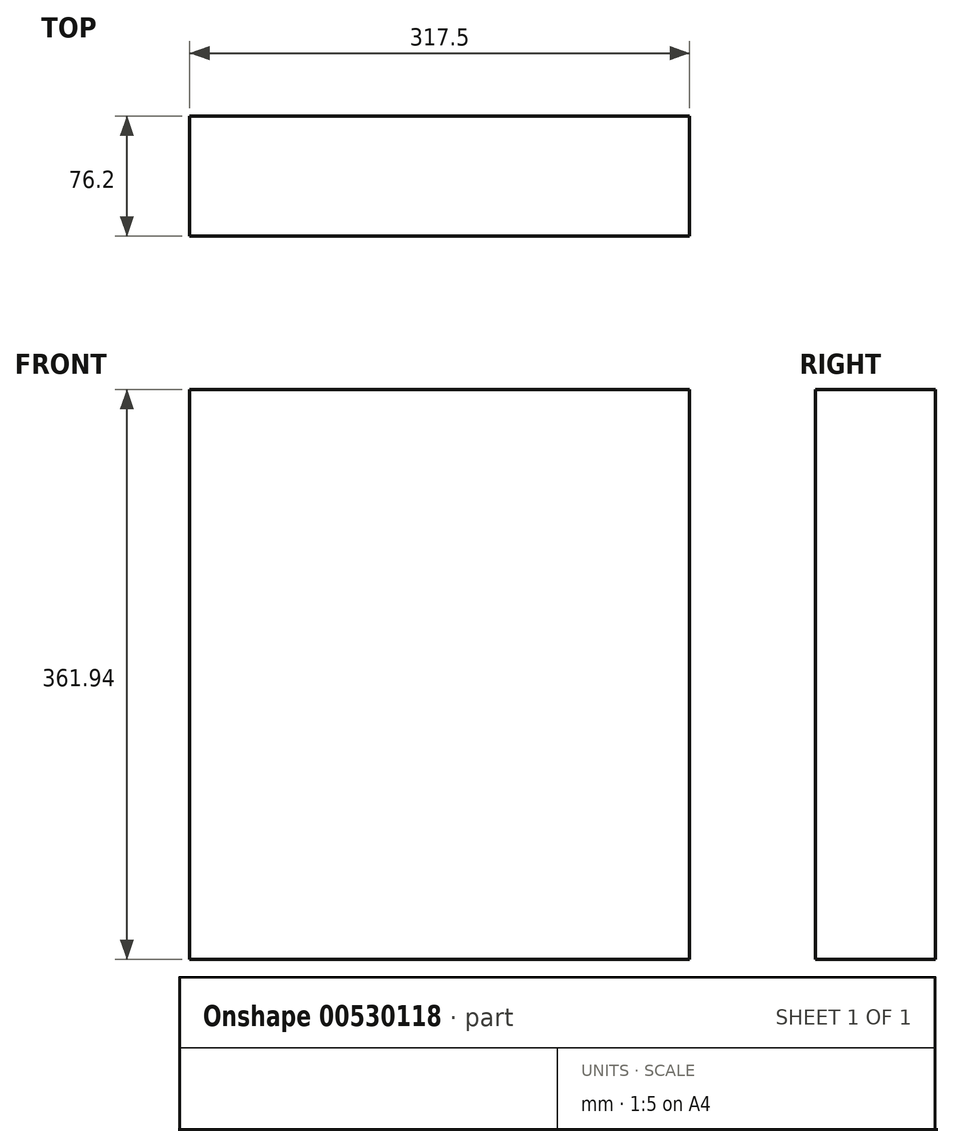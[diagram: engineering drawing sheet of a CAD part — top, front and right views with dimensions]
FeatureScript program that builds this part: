
annotation { "Feature Type Name" : "Feature", "Feature Type Description" : "" }
export const myFeature = defineFeature(function(context is Context, id is Id, definition is map)
    precondition{}
    {
        {
            var Q0;
            Q0=qCreatedBy(makeId("Front.planeOp"),FACE);
            var sketch = newSketch(context, id + "F0", { "sketchPlane" : qUnion([Q0])});
            skLineSegment(sketch, "E0.bottom", {"start": v(-158.75, -180.97) * mm, "end": v(158.75, -180.97) * mm});
            skLineSegment(sketch, "E0.top", {"start": v(-158.75, 180.97) * mm, "end": v(158.75, 180.97) * mm});
            skLineSegment(sketch, "E0.left", {"start": v(-158.75, -180.97) * mm, "end": v(-158.75, 180.97) * mm});
            skLineSegment(sketch, "E0.right", {"start": v(158.75, -180.97) * mm, "end": v(158.75, 180.97) * mm});
            skPoint(sketch, "E0.middle", {"position": v(0, 0) * mm});
            skSolve(sketch);
        }
        {
            var Q0;
            Q0=makeQuery(id+"F0.imprint","IMPRINT",FACE,{"disambiguationData":[TD([[makeQuery(id+"F0.imprint","IMPRINT",EDGE,{"derivedFrom":sQuery(id+"F0.wireOp",EDGE,"E0.bottom")}),1.0]])]});
            extrude(context, id + "F1", {"entities" : qUnion([Q0]), "depth" : 76.2 * mm, "offsetDistance" : 25.4 * mm});
        }
    });
